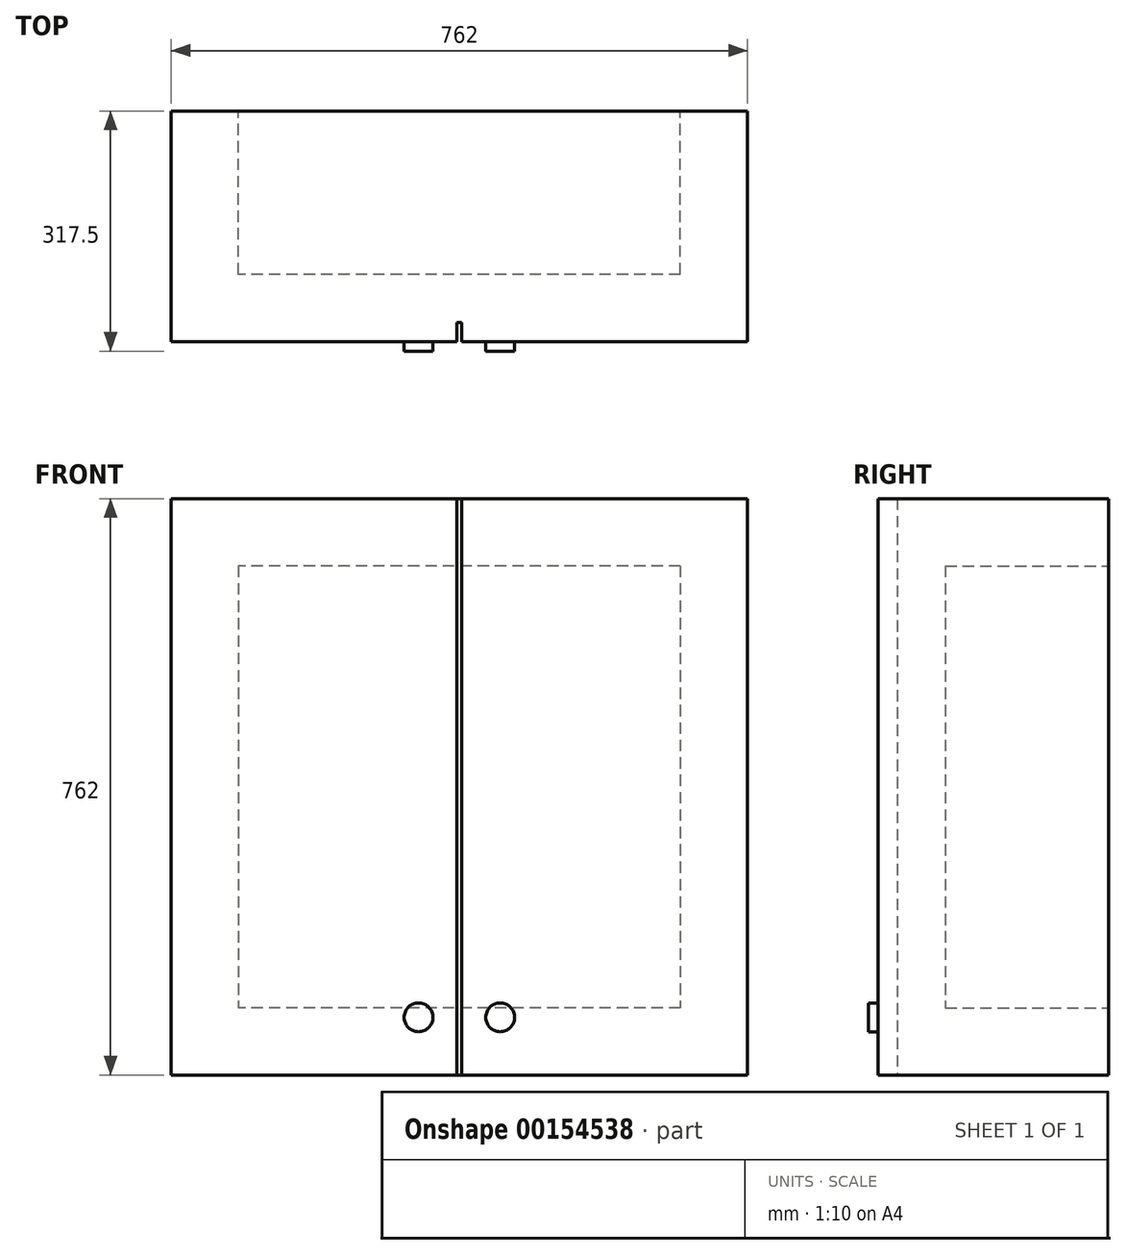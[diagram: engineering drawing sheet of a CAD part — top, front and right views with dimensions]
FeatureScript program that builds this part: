
annotation { "Feature Type Name" : "Feature", "Feature Type Description" : "" }
export const myFeature = defineFeature(function(context is Context, id is Id, definition is map)
    precondition{}
    {
        {
            var Q0;
            Q0=qCreatedBy(makeId("Front.planeOp"),FACE);
            var sketch = newSketch(context, id + "F0", { "sketchPlane" : qUnion([Q0])});
            skLineSegment(sketch, "E0.bottom", {"start": v(0, 0) * mm, "end": v(762, 0) * mm});
            skLineSegment(sketch, "E0.top", {"start": v(0, 762) * mm, "end": v(762, 762) * mm});
            skLineSegment(sketch, "E0.left", {"start": v(0, 0) * mm, "end": v(0, 762) * mm});
            skLineSegment(sketch, "E0.right", {"start": v(762, 0) * mm, "end": v(762, 762) * mm});
            skSolve(sketch);
        }
        {
            var Q0;
            Q0=makeQuery(id+"F0.imprint","IMPRINT",FACE,{"disambiguationData":[TD([[makeQuery(id+"F0.imprint","IMPRINT",EDGE,{"derivedFrom":sQuery(id+"F0.wireOp",EDGE,"E0.bottom")}),1.0]])]});
            extrude(context, id + "F1", {"entities" : qUnion([Q0]), "depth" : 304.8 * mm});
        }
        {
            var Q0;
            Q0=makeQuery(id+"F1.opExtrude","CAP_FACE",FACE,{"disambiguationData":[OSD([sQuery(id+"F0.wireOp",EDGE,"E0.bottom"),sQuery(id+"F0.wireOp",EDGE,"E0.top"),sQuery(id+"F0.wireOp",EDGE,"E0.left"),sQuery(id+"F0.wireOp",EDGE,"E0.right")])],"isStart":false});
            var sketch = newSketch(context, id + "F2", { "sketchPlane" : qUnion([Q0])});
            skLineSegment(sketch, "E1.bottom", {"start": v(377.82, 762) * mm, "end": v(384.18, 762) * mm});
            skLineSegment(sketch, "E1.top", {"start": v(377.83, 0) * mm, "end": v(384.18, 0) * mm});
            skLineSegment(sketch, "E1.left", {"start": v(377.83, 762) * mm, "end": v(377.83, 0) * mm});
            skLineSegment(sketch, "E1.right", {"start": v(384.18, 762) * mm, "end": v(384.18, 0) * mm});
            skLineSegment(sketch, "E2", {"start": v(0, 381) * mm, "end": v(377.83, 381) * mm, "construction": true});
            skLineSegment(sketch, "E3", {"start": v(384.18, 381) * mm, "end": v(762, 381) * mm, "construction": true});
            skSolve(sketch);
        }
        {
            var Q0;
            Q0=makeQuery(id+"F2.imprint","IMPRINT",FACE,{"disambiguationData":[TD([[makeQuery(id+"F2.imprint","IMPRINT",EDGE,{"derivedFrom":sQuery(id+"F2.wireOp",EDGE,"E1.bottom")}),-1.0]])]});
            extrude(context, id + "F3", {"entities" : qUnion([Q0]), "operationType" : NewBodyOperationType.REMOVE, "oppositeDirection" : true, "depth" : 25.4 * mm});
        }
        {
            var Q0;
            {var subQ0=sQuery(id+"F0.wireOp",EDGE,"E0.bottom");var subQ1=sQuery(id+"F0.wireOp",EDGE,"E0.top");var subQ2=sQuery(id+"F0.wireOp",EDGE,"E0.left");Q0=makeQuery(id+"F3.boolean.opBoolean","SPLIT",FACE,{"disambiguationData":[TD([makeQuery(id+"F1.opExtrude","SWEPT_FACE",FACE,{"disambiguationData":[OSD([subQ2])]})])],"derivedFrom":makeQuery(id+"F1.opExtrude","CAP_FACE",FACE,{"disambiguationData":[OSD([subQ0,subQ1,subQ2,sQuery(id+"F0.wireOp",EDGE,"E0.right")])],"isStart":false})});}
            var sketch = newSketch(context, id + "F4", { "sketchPlane" : qUnion([Q0])});
            skCircle(sketch, "E4", {"center": v(327.03, 76.2) * mm, "radius": 19.05 * mm});
            skCircle(sketch, "E5", {"center": v(434.98, 76.2) * mm, "radius": 19.05 * mm});
            skLineSegment(sketch, "E6", {"start": v(377.83, 76.2) * mm, "end": v(327.03, 76.2) * mm, "construction": true});
            skLineSegment(sketch, "E7", {"start": v(434.98, 76.2) * mm, "end": v(384.18, 76.2) * mm, "construction": true});
            skSolve(sketch);
        }
        {
            var Q0;
            Q0=makeQuery(id+"F4.imprint","IMPRINT",FACE,{"disambiguationData":[TD([[makeQuery(id+"F4.imprint","IMPRINT",EDGE,{"derivedFrom":sQuery(id+"F4.wireOp",EDGE,"E4")}),1.0]])]});
            var Q1;
            Q1=makeQuery(id+"F4.imprint","IMPRINT",FACE,{"disambiguationData":[TD([[makeQuery(id+"F4.imprint","IMPRINT",EDGE,{"derivedFrom":sQuery(id+"F4.wireOp",EDGE,"E5")}),1.0]])]});
            extrude(context, id + "F5", {"entities" : qUnion([Q0, Q1]), "operationType" : NewBodyOperationType.ADD, "depth" : 12.7 * mm});
        }
        {
            var Q0;
            Q0=makeQuery(id+"F1.opExtrude","CAP_FACE",FACE,{"disambiguationData":[OSD([sQuery(id+"F0.wireOp",EDGE,"E0.bottom"),sQuery(id+"F0.wireOp",EDGE,"E0.top"),sQuery(id+"F0.wireOp",EDGE,"E0.left"),sQuery(id+"F0.wireOp",EDGE,"E0.right")])],"isStart":true});
            var sketch = newSketch(context, id + "F6", { "sketchPlane" : qUnion([Q0])});
            skLineSegment(sketch, "E8.bottom", {"start": v(-673.1, 673.1) * mm, "end": v(-88.9, 673.1) * mm});
            skLineSegment(sketch, "E8.top", {"start": v(-673.1, 88.9) * mm, "end": v(-88.9, 88.9) * mm});
            skLineSegment(sketch, "E8.left", {"start": v(-673.1, 673.1) * mm, "end": v(-673.1, 88.9) * mm});
            skLineSegment(sketch, "E8.right", {"start": v(-88.9, 673.1) * mm, "end": v(-88.9, 88.9) * mm});
            skSolve(sketch);
        }
        {
            var Q0;
            Q0=makeQuery(id+"F6.imprint","IMPRINT",FACE,{"disambiguationData":[TD([[makeQuery(id+"F6.imprint","IMPRINT",EDGE,{"derivedFrom":sQuery(id+"F6.wireOp",EDGE,"E8.bottom")}),-1.0]])]});
            extrude(context, id + "F7", {"entities" : qUnion([Q0]), "operationType" : NewBodyOperationType.REMOVE, "oppositeDirection" : true, "depth" : 215.9 * mm});
        }
    });
